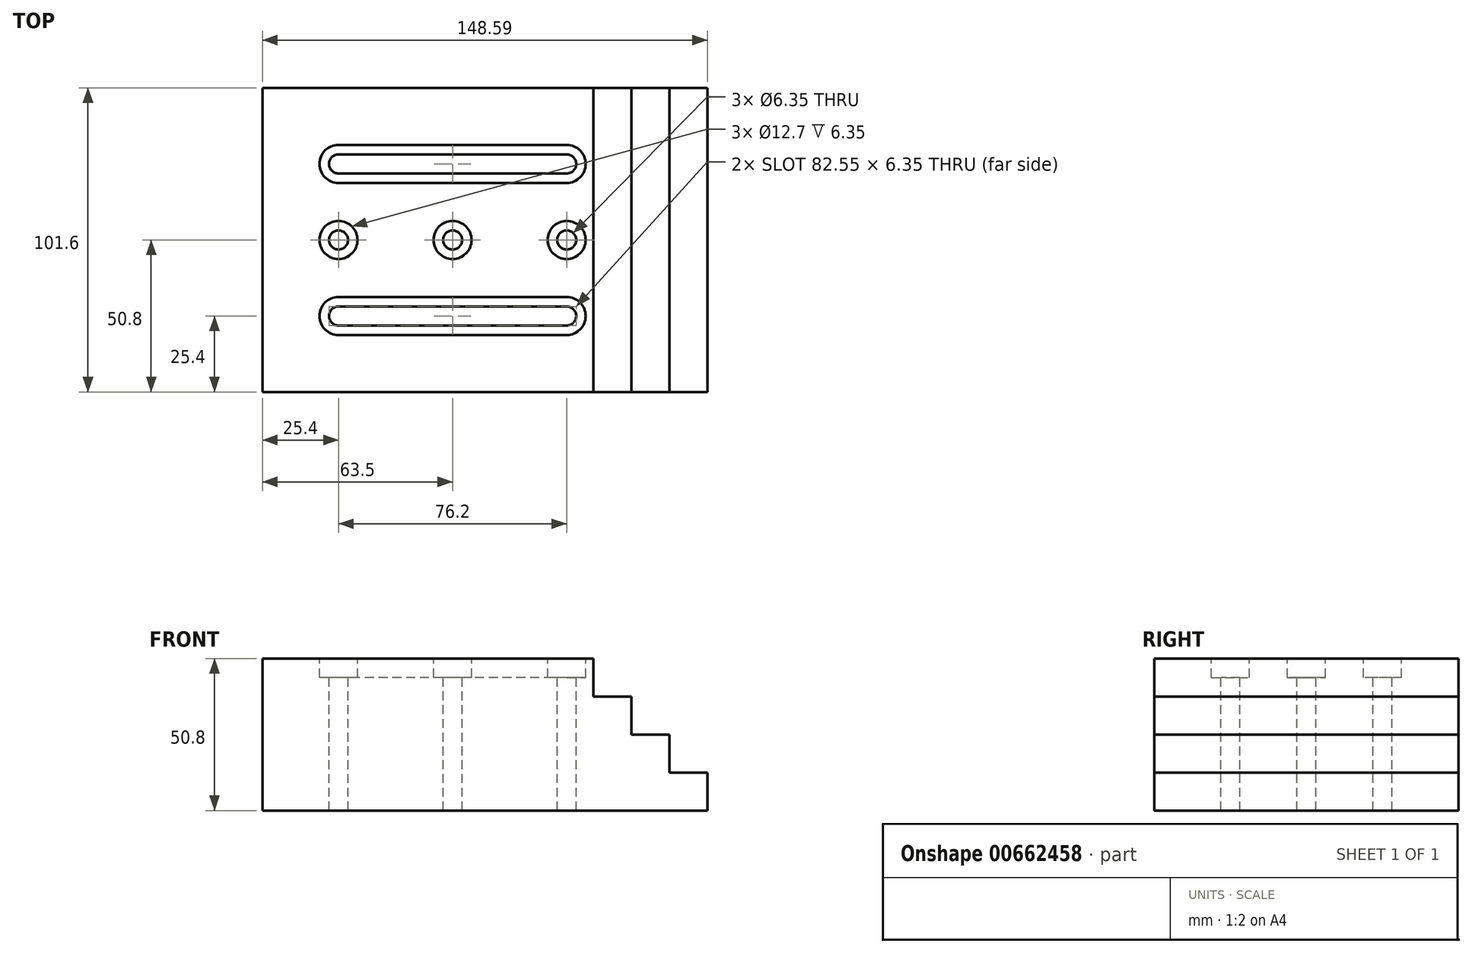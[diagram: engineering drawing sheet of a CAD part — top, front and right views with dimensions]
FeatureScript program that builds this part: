
annotation { "Feature Type Name" : "Feature", "Feature Type Description" : "" }
export const myFeature = defineFeature(function(context is Context, id is Id, definition is map)
    precondition{}
    {
        {
            var Q0;
            Q0=qCreatedBy(makeId("Front.planeOp"),FACE);
            var sketch = newSketch(context, id + "F0", { "sketchPlane" : qUnion([Q0])});
            skLineSegment(sketch, "E0", {"start": v(0, 0) * mm, "end": v(0, 50.8) * mm});
            skLineSegment(sketch, "E1", {"start": v(0, 50.8) * mm, "end": v(110.5, 50.8) * mm});
            skLineSegment(sketch, "E2", {"start": v(110.5, 50.8) * mm, "end": v(110.5, 38.1) * mm});
            skLineSegment(sketch, "E3", {"start": v(110.5, 38.1) * mm, "end": v(123.19, 38.1) * mm});
            skLineSegment(sketch, "E4", {"start": v(123.19, 38.1) * mm, "end": v(123.19, 25.4) * mm});
            skLineSegment(sketch, "E5", {"start": v(123.19, 25.4) * mm, "end": v(135.89, 25.4) * mm});
            skLineSegment(sketch, "E6", {"start": v(135.89, 25.4) * mm, "end": v(135.89, 12.7) * mm});
            skLineSegment(sketch, "E7", {"start": v(135.89, 12.7) * mm, "end": v(148.59, 12.7) * mm});
            skLineSegment(sketch, "E8", {"start": v(148.59, 12.7) * mm, "end": v(148.59, 0) * mm});
            skLineSegment(sketch, "E9", {"start": v(148.59, 0) * mm, "end": v(0, 0) * mm});
            skSolve(sketch);
        }
        {
            var Q0;
            Q0 = qSketchRegion(id + "F0", true);
            extrude(context, id + "F1", {"entities" : qUnion([Q0]), "depth" : 101.6 * mm, "offsetDistance" : 25.4 * mm});
        }
        {
            var Q0;
            Q0=makeQuery(id+"F1.opExtrude","SWEPT_FACE",FACE,{"disambiguationData":[OSD([sQuery(id+"F0.wireOp",EDGE,"E1")])]});
            var sketch = newSketch(context, id + "F2", { "sketchPlane" : qUnion([Q0])});
            skCircle(sketch, "E10", {"center": v(25.4, -25.4) * mm, "radius": 6.35 * mm});
            skCircle(sketch, "E11", {"center": v(101.6, -25.4) * mm, "radius": 6.35 * mm});
            skLineSegment(sketch, "E12", {"start": v(101.6, -19.05) * mm, "end": v(25.4, -19.05) * mm});
            skLineSegment(sketch, "E13", {"start": v(25.4, -31.75) * mm, "end": v(101.6, -31.75) * mm});
            skLineSegment(sketch, "E14.0.1.0", {"start": v(25.4, -82.55) * mm, "end": v(101.6, -82.55) * mm});
            skCircle(sketch, "E14.0.1.1", {"center": v(101.6, -76.2) * mm, "radius": 6.35 * mm});
            skLineSegment(sketch, "E14.0.1.2", {"start": v(101.6, -69.85) * mm, "end": v(25.4, -69.85) * mm});
            skCircle(sketch, "E14.0.1.3", {"center": v(25.4, -76.2) * mm, "radius": 6.35 * mm});
            skLineSegment(sketch, "E14.1.1.0", {"start": v(25.4, -82.55) * mm, "end": v(101.6, -82.55) * mm});
            skCircle(sketch, "E14.1.1.1", {"center": v(101.6, -76.2) * mm, "radius": 6.35 * mm});
            skLineSegment(sketch, "E14.1.1.2", {"start": v(101.6, -69.85) * mm, "end": v(25.4, -69.85) * mm});
            skCircle(sketch, "E14.1.1.3", {"center": v(25.4, -76.2) * mm, "radius": 6.35 * mm});
            skLineSegment(sketch, "E14.2.1.0", {"start": v(25.4, -82.55) * mm, "end": v(101.6, -82.55) * mm});
            skCircle(sketch, "E14.2.1.1", {"center": v(101.6, -76.2) * mm, "radius": 6.35 * mm});
            skLineSegment(sketch, "E14.2.1.2", {"start": v(101.6, -69.85) * mm, "end": v(25.4, -69.85) * mm});
            skCircle(sketch, "E14.2.1.3", {"center": v(25.4, -76.2) * mm, "radius": 6.35 * mm});
            skLineSegment(sketch, "E14.direction1", {"start": v(25.4, -31.75) * mm, "end": v(25.4, -31.75) * mm});
            skLineSegment(sketch, "E14.direction2", {"start": v(25.4, -31.75) * mm, "end": v(25.4, -82.55) * mm, "construction": true});
            skSolve(sketch);
        }
        {
            var Q0;
            Q0 = qSketchRegion(id + "F2", true);
            extrude(context, id + "F3", {"entities" : qUnion([Q0]), "operationType" : NewBodyOperationType.REMOVE, "oppositeDirection" : true, "depth" : 6.35 * mm, "offsetDistance" : 25.4 * mm});
        }
        {
            var Q0;
            Q0=makeQuery(id+"F1.opExtrude","SWEPT_FACE",FACE,{"disambiguationData":[OSD([sQuery(id+"F0.wireOp",EDGE,"E1")])]});
            var sketch = newSketch(context, id + "F4", { "sketchPlane" : qUnion([Q0])});
            skCircle(sketch, "E15", {"center": v(101.6, -50.8) * mm, "radius": 3.18 * mm});
            skCircle(sketch, "E16.1.0.0", {"center": v(63.5, -50.8) * mm, "radius": 3.18 * mm});
            skLineSegment(sketch, "E16.direction1", {"start": v(101.6, -50.8) * mm, "end": v(63.5, -50.8) * mm, "construction": true});
            skCircle(sketch, "E17", {"center": v(25.4, -25.4) * mm, "radius": 3.18 * mm});
            skCircle(sketch, "E18.0.2.0", {"center": v(25.4, -50.8) * mm, "radius": 3.18 * mm});
            skCircle(sketch, "E19.0.1.0", {"center": v(25.4, -76.2) * mm, "radius": 3.18 * mm});
            skCircle(sketch, "E19.1.0.0", {"center": v(101.6, -25.4) * mm, "radius": 3.18 * mm});
            skCircle(sketch, "E19.1.1.0", {"center": v(101.6, -76.2) * mm, "radius": 3.18 * mm});
            skLineSegment(sketch, "E20", {"start": v(25.4, -22.23) * mm, "end": v(101.6, -22.23) * mm});
            skLineSegment(sketch, "E21", {"start": v(101.6, -28.58) * mm, "end": v(25.4, -28.58) * mm});
            skLineSegment(sketch, "E22", {"start": v(25.4, -73.03) * mm, "end": v(101.6, -73.03) * mm});
            skLineSegment(sketch, "E23", {"start": v(101.6, -79.38) * mm, "end": v(25.4, -79.37) * mm});
            skSolve(sketch);
        }
        {
            var Q0;
            Q0 = qSketchRegion(id + "F4", true);
            extrude(context, id + "F5", {"entities" : qUnion([Q0]), "operationType" : NewBodyOperationType.REMOVE, "endBound" : BoundingType.THROUGH_ALL, "oppositeDirection" : true, "depth" : 25.4 * mm, "offsetDistance" : 25.4 * mm});
        }
        {
            var Q0;
            Q0=makeQuery(id+"F1.opExtrude","SWEPT_FACE",FACE,{"disambiguationData":[OSD([sQuery(id+"F0.wireOp",EDGE,"E1")])]});
            var sketch = newSketch(context, id + "F6", { "sketchPlane" : qUnion([Q0])});
            skCircle(sketch, "E24", {"center": v(101.6, -50.8) * mm, "radius": 6.35 * mm});
            skCircle(sketch, "E25.1.0.0", {"center": v(63.5, -50.8) * mm, "radius": 6.35 * mm});
            skCircle(sketch, "E25.1.1.0", {"center": v(63.5, -50.8) * mm, "radius": 6.35 * mm});
            skCircle(sketch, "E25.2.0.0", {"center": v(25.4, -50.8) * mm, "radius": 6.35 * mm});
            skCircle(sketch, "E25.2.1.0", {"center": v(25.4, -50.8) * mm, "radius": 6.35 * mm});
            skLineSegment(sketch, "E25.direction1", {"start": v(101.6, -50.8) * mm, "end": v(63.5, -50.8) * mm, "construction": true});
            skLineSegment(sketch, "E25.direction2", {"start": v(101.6, -50.8) * mm, "end": v(101.6, -50.8) * mm});
            skSolve(sketch);
        }
        {
            var Q0;
            Q0 = qSketchRegion(id + "F6", true);
            extrude(context, id + "F7", {"entities" : qUnion([Q0]), "operationType" : NewBodyOperationType.REMOVE, "oppositeDirection" : true, "depth" : 6.35 * mm, "offsetDistance" : 25.4 * mm});
        }
    });
